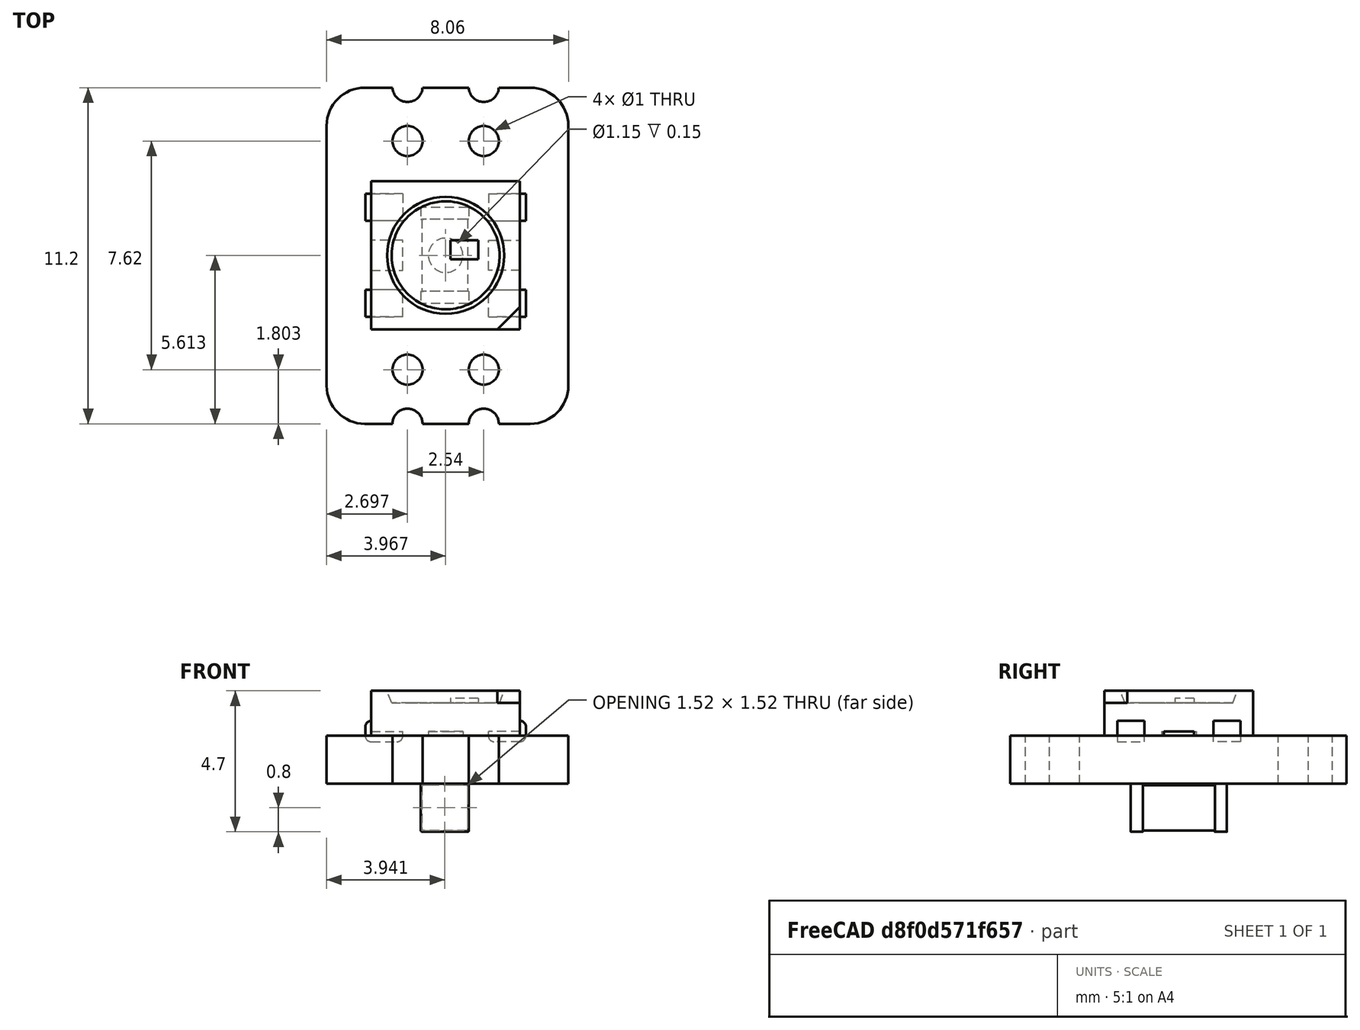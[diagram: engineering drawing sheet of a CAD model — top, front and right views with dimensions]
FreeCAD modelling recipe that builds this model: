
FCSTD DOCUMENT  (FreeCAD 0.16R6712 (Git))
Label: ws2812b_reverse1
License: All rights reserved
LicenseURL: http://en.wikipedia.org/wiki/All_rights_reserved
objects: Part::Feature×3, App::DocumentObjectGroup×2, Sketcher::SketchObject×1
note: 4 computed .brp shape members not serialized (recipe doc carries the construction recipe); baked Part::Feature solids carry a one-line shape summary decoded from their .brp

FEATURE [Part::Feature] Pcb
  Placement = pos=(-144.208,107.328,0) rot=(0,0,1;0rad)
  shape: bbox 8.072 x 11.22 x 1.62 mm, 24 faces (baked)
FEATURE [Sketcher::SketchObject] PCB_Sketch
  sketch-geometry (8):
    g0: LineSegment StartX=4.0259 StartY=-4.3307 StartZ=0 EndX=4.0259 EndY=4.3307 EndZ=0
    g1: LineSegment StartX=-2.7559 StartY=-5.6007 StartZ=0 EndX=2.7559 EndY=-5.6007 EndZ=0
    g2: LineSegment StartX=-4.0259 StartY=4.3307 StartZ=0 EndX=-4.0259 EndY=-4.3307 EndZ=0
    g3: LineSegment StartX=2.7559 StartY=5.6007 StartZ=0 EndX=-2.7559 EndY=5.6007 EndZ=0
    g4: ArcOfCircle CenterX=2.7559 CenterY=-4.3307 CenterZ=0 NormalX=0 NormalY=0 NormalZ=1 Radius=1.27 StartAngle=4.71239 EndAngle=6.28319
    g5: ArcOfCircle CenterX=-2.7559 CenterY=-4.3307 CenterZ=0 NormalX=0 NormalY=0 NormalZ=1 Radius=1.27 StartAngle=3.14159 EndAngle=4.71239
    g6: ArcOfCircle CenterX=-2.7559 CenterY=4.3307 CenterZ=0 NormalX=0 NormalY=0 NormalZ=1 Radius=1.27 StartAngle=1.5708 EndAngle=3.14159
    g7: ArcOfCircle CenterX=2.7559 CenterY=4.3307 CenterZ=0 NormalX=0 NormalY=0 NormalZ=1 Radius=1.27 StartAngle=0 EndAngle=1.5708
FEATURE [App::DocumentObjectGroup] Board_Geoms
  Group = -> [Pcb,PCB_Sketch]
FEATURE [Part::Feature] Shape  label="risk1E78E08Bni4a_"
  Placement = pos=(-0.0635,0.0127,0) rot=(0,0,-1;1.5708rad)
  shape: bbox 5.35 x 4.95 x 1.7 mm, 58 faces (baked)
FEATURE [Part::Feature] Shape001  label="C_1206_3216Metric_"
  Placement = pos=(-0.0889,0.0127,-1.6) rot=(-0.707107,0.707107,0;3.14159rad)
  shape: bbox 1.6 x 3.2 x 1.6 mm, 28 faces (baked)
FEATURE [App::DocumentObjectGroup] Step_Models
  Group = -> [Shape,Shape001]
